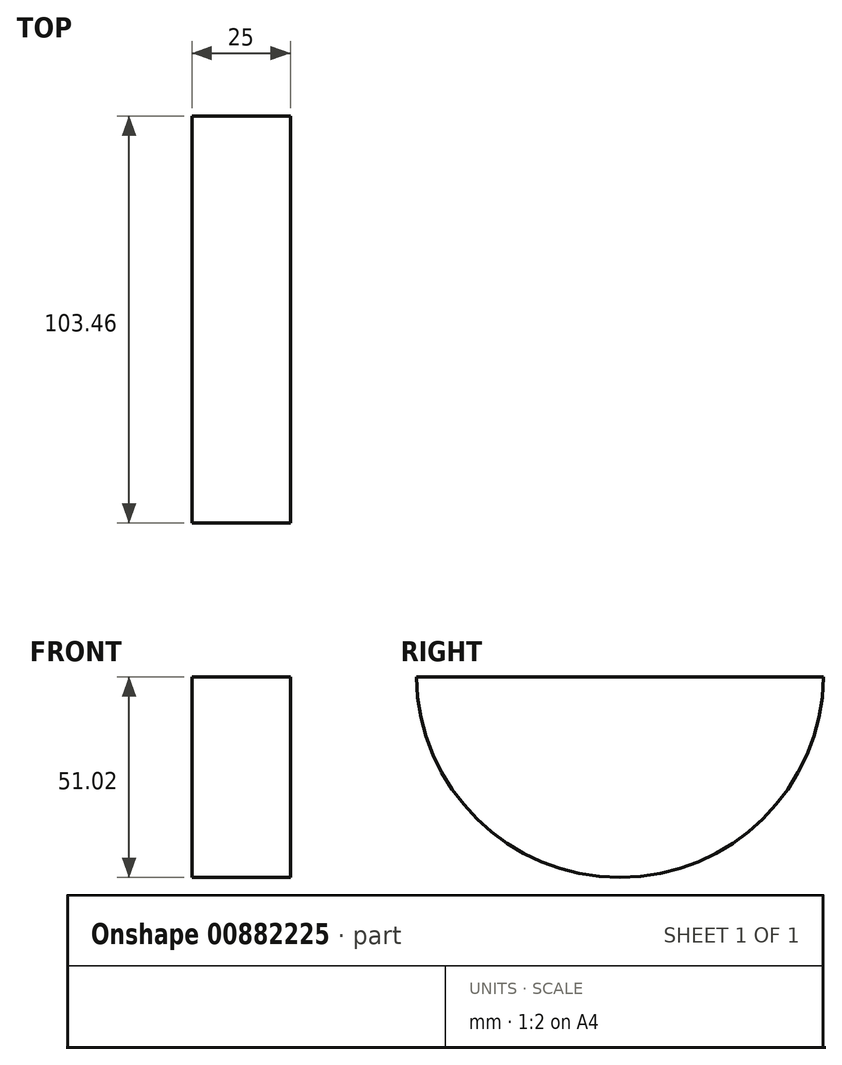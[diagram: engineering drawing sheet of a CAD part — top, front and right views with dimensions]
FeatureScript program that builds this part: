
annotation { "Feature Type Name" : "Feature", "Feature Type Description" : "" }
export const myFeature = defineFeature(function(context is Context, id is Id, definition is map)
    precondition{}
    {
        {
            var Q0;
            Q0=qCreatedBy(makeId("Right.planeOp"),FACE);
            var sketch = newSketch(context, id + "F0", { "sketchPlane" : qUnion([Q0])});
            skArc(sketch, "E0", {"start": v(-44.4, 0) * mm, "mid": v(7.33, -51.02) * mm, "end": v(59.06, 0) * mm});
            skLineSegment(sketch, "E1", {"start": v(59.06, 0) * mm, "end": v(-44.4, 0) * mm});
            skLineSegment(sketch, "E2", {"start": v(-5.9, 0) * mm, "end": v(-5.9, 28.02) * mm});
            skLineSegment(sketch, "E3", {"start": v(7.33, 0.72) * mm, "end": v(7.33, 28.02) * mm});
            skLineSegment(sketch, "E4", {"start": v(7.33, 28.02) * mm, "end": v(-5.9, 28.02) * mm});
            skSolve(sketch);
        }
        {
            var Q0;
            {var subQ0=sQuery(id+"F0.wireOp",EDGE,"E0");Q0=makeQuery(id+"F0.imprint","IMPRINT",FACE,{"disambiguationData":[TD([[makeQuery(id+"F0.imprint","IMPRINT",EDGE,{"derivedFrom":subQ0}),1.0]])]});}
            extrude(context, id + "F1", {"entities" : qUnion([Q0]), "depth" : 25 * mm, "offsetDistance" : 25 * mm});
        }
    });
